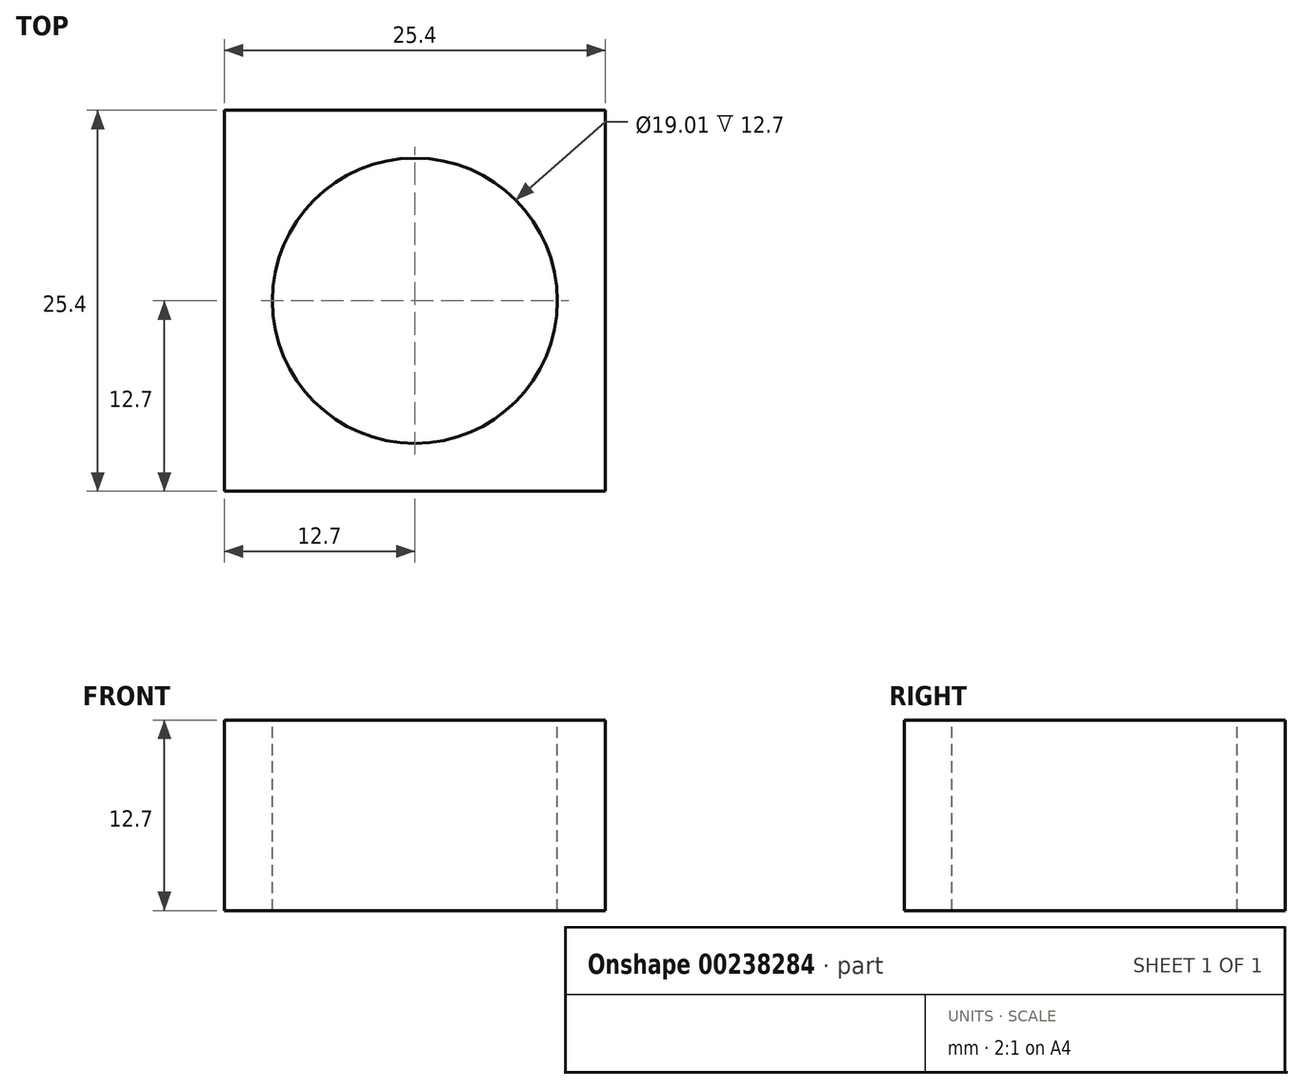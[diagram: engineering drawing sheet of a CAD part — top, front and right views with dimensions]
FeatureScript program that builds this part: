
annotation { "Feature Type Name" : "Feature", "Feature Type Description" : "" }
export const myFeature = defineFeature(function(context is Context, id is Id, definition is map)
    precondition{}
    {
        {
            var Q0;
            Q0=qCreatedBy(makeId("Top.planeOp"),FACE);
            var sketch = newSketch(context, id + "F0", { "sketchPlane" : qUnion([Q0])});
            skLineSegment(sketch, "E0.bottom", {"start": v(0, 0) * mm, "end": v(25.4, 0) * mm});
            skLineSegment(sketch, "E0.top", {"start": v(0, 25.4) * mm, "end": v(25.4, 25.4) * mm});
            skLineSegment(sketch, "E0.left", {"start": v(0, 0) * mm, "end": v(0, 25.4) * mm});
            skLineSegment(sketch, "E0.right", {"start": v(25.4, 0) * mm, "end": v(25.4, 25.4) * mm});
            skSolve(sketch);
        }
        {
            var Q0;
            Q0 = qSketchRegion(id + "F0", true);
            extrude(context, id + "F1", {"entities" : qUnion([Q0]), "depth" : 12.7 * mm});
        }
        {
            var Q0;
            Q0=makeQuery(id+"F1.opExtrude","CAP_FACE",FACE,{"disambiguationData":[OSD([sQuery(id+"F0.wireOp",EDGE,"E0.bottom"),sQuery(id+"F0.wireOp",EDGE,"E0.top"),sQuery(id+"F0.wireOp",EDGE,"E0.left"),sQuery(id+"F0.wireOp",EDGE,"E0.right")])],"isStart":false});
            var sketch = newSketch(context, id + "F2", { "sketchPlane" : qUnion([Q0])});
            skCircle(sketch, "E1", {"center": v(12.7, 12.7) * mm, "radius": 9.5 * mm});
            skPoint(sketch, "E1.centerSnap0", {"position": v(25.4, 12.7) * mm});
            skPoint(sketch, "E1.centerSnap1", {"position": v(12.7, 0) * mm});
            skSolve(sketch);
        }
        {
            var Q0;
            Q0=makeQuery(id+"F2.imprint","IMPRINT",FACE,{"disambiguationData":[TD([[makeQuery(id+"F2.imprint","IMPRINT",EDGE,{"derivedFrom":sQuery(id+"F2.wireOp",EDGE,"E1")}),1.0]])]});
            extrude(context, id + "F3", {"entities" : qUnion([Q0]), "operationType" : NewBodyOperationType.REMOVE, "oppositeDirection" : true, "depth" : 12.7 * mm});
        }
    });
